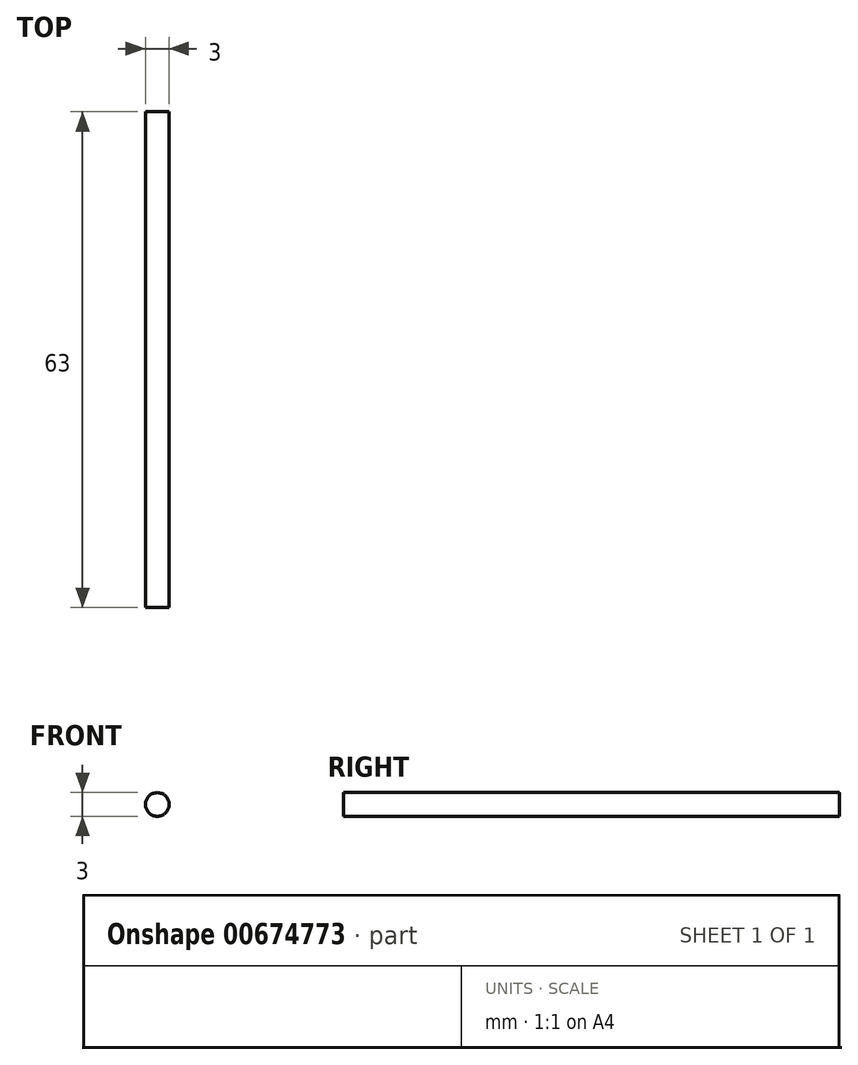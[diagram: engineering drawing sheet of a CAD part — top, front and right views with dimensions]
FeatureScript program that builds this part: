
annotation { "Feature Type Name" : "Feature", "Feature Type Description" : "" }
export const myFeature = defineFeature(function(context is Context, id is Id, definition is map)
    precondition{}
    {
        {
            var Q0;
            Q0=qCreatedBy(makeId("Front.planeOp"),FACE);
            var sketch = newSketch(context, id + "F0", { "sketchPlane" : qUnion([Q0])});
            skCircle(sketch, "E0", {"center": v(0, 0) * mm, "radius": 1.5 * mm});
            skSolve(sketch);
        }
        {
            var Q0;
            Q0=makeQuery(id+"F0.imprint","IMPRINT",FACE,{"disambiguationData":[TD([[makeQuery(id+"F0.imprint","IMPRINT",EDGE,{"derivedFrom":sQuery(id+"F0.wireOp",EDGE,"E0")}),1.0]])]});
            extrude(context, id + "F1", {"entities" : qUnion([Q0]), "depth" : 63 * mm, "offsetDistance" : 25.4 * mm});
        }
    });
